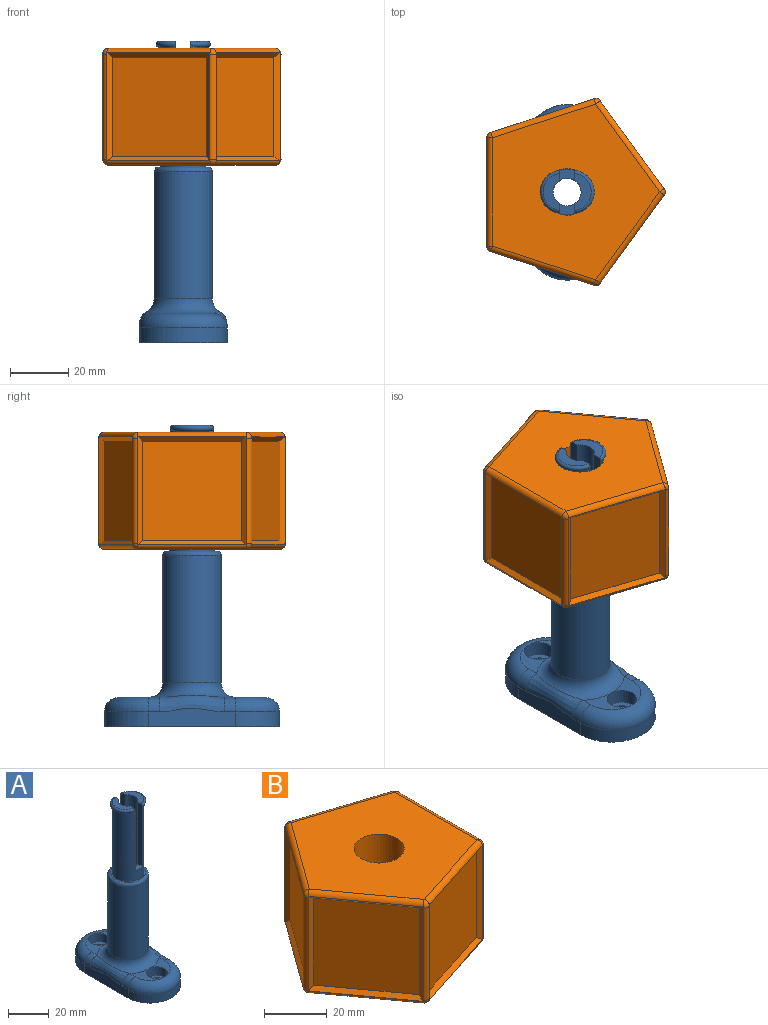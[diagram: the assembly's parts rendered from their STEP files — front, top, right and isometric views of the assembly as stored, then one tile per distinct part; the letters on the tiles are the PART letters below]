
ASSEMBLY  parts=2 mates=1
PART A: 44 faces, bbox 40.2x62.5x103 mm
  f0: cylinder r=4.75mm len=103mm, axis (0,0,-1), area 2685mm2, adj f12,f15,f16,f17,f18,f19,f20,f21
  f1: cylinder r=7.75mm len=42mm, axis (0,0,-1), area 1636.6mm2, adj f14,f15,f16,f17,f18,f19,f20,f22
  f2: plane 13.82x10mm, normal (0,0,1), area 51.3mm2, adj f29,f31,f34,f36
  f3: plane 13.82x10mm, normal (0,0,1), area 51.3mm2, adj f27,f31,f39,f40
  f4: plane 13.82x10mm, normal (0,0,1), area 51.3mm2, adj f29,f31,f33,f34
  f5: cylinder r=3mm len=6mm, axis (0,0,-1), area 94.2mm2, adj f12,f30
  f6: cylinder r=3mm len=6mm, axis (0,0,-1), area 94.2mm2, adj f12,f28
  f7: plane 30x6.34mm, normal (1,0,0), area 164.8mm2, adj f8,f10,f12,f36,f38,f40
  f8: cylinder r=15mm len=30mm, axis (0,0,-1), area 235.6mm2, adj f7,f9,f12,f39
  f9: plane 30x6.34mm, normal (-1,0,0), area 164.8mm2, adj f8,f10,f12,f33,f35,f37
  f10: cylinder r=15mm len=30mm, axis (0,0,-1), area 235.6mm2, adj f7,f9,f12,f34
  f11: plane 13.82x10mm, normal (0,0,1), area 51.3mm2, adj f27,f31,f37,f39
  f12: plane 60x30mm, normal (0,0,-1), area 1479.4mm2, adj f0,f5,f6,f7,f8,f9,f10
  f13: cylinder r=10mm len=43.5mm, axis (0,0,-1), area 2733.2mm2, adj f31,f32
  f14: plane 17x17mm, normal (0,0,1), area 38.3mm2, adj f1,f32
  f15: plane 5x3.71mm, normal (0,0,1), area 15.5mm2, adj f0,f1,f16,f17
  f16: plane 37.04x3.34mm, normal (1,0,0), area 121.8mm2, adj f0,f1,f15,f23,f26
  f17: plane 37.04x3.34mm, normal (-1,0,0), area 121.8mm2, adj f0,f1,f15,f21,f25
  f18: plane 5x3.71mm, normal (0,0,1), area 15.5mm2, adj f0,f1,f19,f20
  f19: plane 37.04x3.34mm, normal (-1,0,0), area 120.9mm2, adj f0,f1,f18,f21,f25,f41
  f20: plane 37.04x3.34mm, normal (1,0,0), area 121.8mm2, adj f0,f1,f18,f23,f26
  f21: plane 12.66x5.75mm, normal (0,0,1), area 43mm2, adj f0,f17,f19,f25
  f22: plane 9.48x2.12mm, normal (0,0,-1), area 3.4mm2, adj f1,f25
  f23: plane 12.66x5.75mm, normal (0,0,1), area 43mm2, adj f0,f16,f20,f26
  f24: plane 9.48x2.12mm, normal (0,0,-1), area 3.4mm2, adj f1,f26
  f25: torus R=6.36mm, axis (0,0,1), area 60.7mm2, adj f1,f17,f19,f21,f22
  f26: torus R=6.36mm, axis (0,0,1), area 60.7mm2, adj f1,f16,f20,f23,f24
  f27: cylinder r=5mm len=10mm, axis (0,0,1), area 157.1mm2, adj f3,f11,f28
  f28: plane 10x10mm, normal (0,0,1), area 50.3mm2, adj f6,f27
  f29: cylinder r=5mm len=10mm, axis (0,0,1), area 157.1mm2, adj f2,f4,f30
  f30: plane 10x10mm, normal (0,0,1), area 50.3mm2, adj f5,f29
  f31: torus R=15mm, axis (0,0,1), area 496.9mm2, adj f2,f3,f4,f11,f13,f35,f38
  f32: torus R=8.5mm, axis (0,0,1), area 140mm2, adj f13,f14
  f33: cylinder r=5mm len=5mm, axis (0,1,0), area 30mm2, adj f4,f9,f34,f35
  f34: torus R=10mm, axis (0,0,1), area 325.3mm2, adj f2,f4,f10,f33,f36
  f35: bspline ~25.73x5.67mm, area 140.1mm2, adj f9,f31,f33,f37
  f36: cylinder r=5mm len=5mm, axis (0,-1,0), area 30mm2, adj f2,f7,f34,f38
  f37: cylinder r=5mm len=5mm, axis (0,1,0), area 30mm2, adj f9,f11,f35,f39
  f38: bspline ~25.73x5.67mm, area 140.1mm2, adj f7,f31,f36,f40
  f39: torus R=10mm, axis (0,0,1), area 325.3mm2, adj f3,f8,f11,f37,f40
  f40: cylinder r=5mm len=5mm, axis (0,-1,0), area 30mm2, adj f3,f7,f38,f39
  f41: cylinder r=1.5mm len=2.07mm, axis (-0.71,-0.71,0), area 0.6mm2, adj f0,f19
  f42: plane 1.68x0.99mm, normal (0.71,0.71,0), area 1.8mm2, adj f43
  f43: bspline ~3x2.13mm, area 6mm2, adj f1,f42
PART B: 65 faces, bbox 61.1x64x40 mm
  f0: cylinder r=8mm len=40mm, axis (0,0,-1), area 2003.5mm2, adj f11,f12,f63
  f1: plane 36x0.04mm, normal (0.31,-0.95,0), area 1.7mm2, adj f21,f42,f43,f53
  f2: plane 36x0.04mm, normal (-0.81,-0.59,0), area 1.7mm2, adj f25,f41,f47,f56
  f3: plane 36x0.05mm, normal (1,0,0), area 1.7mm2, adj f37,f38,f46,f57
  f4: plane 36x0.04mm, normal (-0.81,0.59,0), area 1.7mm2, adj f29,f40,f51,f60
  f5: plane 36x0.04mm, normal (0.31,0.95,0), area 1.7mm2, adj f33,f39,f50,f61
  f6: plane 36x0.04mm, normal (0.31,-0.95,0), area 1.7mm2, adj f18,f41,f43,f53
  f7: plane 36x0.04mm, normal (-0.81,-0.59,0), area 1.7mm2, adj f22,f40,f47,f56
  f8: plane 36x0.04mm, normal (-0.81,0.59,0), area 1.7mm2, adj f26,f39,f51,f60
  f9: plane 36x0.04mm, normal (0.31,0.95,0), area 1.7mm2, adj f30,f38,f50,f61
  f10: plane 36x0.05mm, normal (1,0,0), area 1.7mm2, adj f34,f42,f46,f57
  f11: plane 60.02x57.08mm, normal (0,0,1), area 2166.2mm2, adj f0,f43,f46,f47,f50,f51
  f12: plane 60.02x57.08mm, normal (0,0,-1), area 2166.2mm2, adj f0,f53,f56,f57,f60,f61
  f13: plane 34x34mm, normal (1,0,0), area 1156mm2, adj f34,f35,f36,f37
  f14: plane 34x32.34mm, normal (0.31,0.95,0), area 1156mm2, adj f30,f31,f32,f33
  f15: plane 34x27.51mm, normal (-0.81,0.59,0), area 1156mm2, adj f26,f27,f28,f29
  f16: plane 34x27.51mm, normal (-0.81,-0.59,0), area 1156mm2, adj f22,f23,f24,f25
  f17: plane 34x32.34mm, normal (0.31,-0.95,0), area 1156mm2, adj f18,f19,f20,f21
  f18: plane 36.9x1.89mm, normal (0.89,-0.45,0), area 75.3mm2, adj f6,f17,f19,f20,f43,f53
  f19: plane 35.09x12.33mm, normal (0.22,-0.67,-0.71), area 72.6mm2, adj f17,f18,f21,f43
  f20: plane 35.09x12.33mm, normal (0.22,-0.67,0.71), area 72.6mm2, adj f17,f18,f21,f53
  f21: plane 36.9x1.89mm, normal (-0.45,-0.89,0), area 75.3mm2, adj f1,f17,f19,f20,f43,f53
  f22: plane 36.9x2.1mm, normal (-0.16,-0.99,0), area 75.3mm2, adj f7,f16,f23,f24,f47,f56
  f23: plane 29.85x22.01mm, normal (-0.57,-0.42,-0.71), area 72.6mm2, adj f16,f22,f25,f47
  f24: plane 29.85x22.01mm, normal (-0.57,-0.42,0.71), area 72.6mm2, adj f16,f22,f25,f56
  f25: plane 36.9x2.1mm, normal (-0.99,0.16,0), area 75.3mm2, adj f2,f16,f23,f24,f47,f56
  f26: plane 36.9x2.1mm, normal (-0.99,-0.16,0), area 75.3mm2, adj f8,f15,f27,f28,f51,f60
  f27: plane 29.85x22.01mm, normal (-0.57,0.42,-0.71), area 72.6mm2, adj f15,f26,f29,f51
  f28: plane 29.85x22.01mm, normal (-0.57,0.42,0.71), area 72.6mm2, adj f15,f26,f29,f60
  f29: plane 36.9x2.1mm, normal (-0.16,0.99,0), area 75.3mm2, adj f4,f15,f27,f28,f51,f60
  f30: plane 36.9x1.89mm, normal (-0.45,0.89,0), area 75.3mm2, adj f9,f14,f31,f32,f50,f61
  f31: plane 35.09x12.33mm, normal (0.22,0.67,-0.71), area 72.6mm2, adj f14,f30,f33,f50
  f32: plane 35.09x12.33mm, normal (0.22,0.67,0.71), area 72.6mm2, adj f14,f30,f33,f61
  f33: plane 36.9x1.89mm, normal (0.89,0.45,0), area 75.3mm2, adj f5,f14,f31,f32,f50,f61
  f34: plane 36.9x1.5mm, normal (0.71,0.71,0), area 75.3mm2, adj f10,f13,f35,f36,f46,f57
  f35: plane 36.9x1.45mm, normal (0.71,0,-0.71), area 72.6mm2, adj f13,f34,f37,f46
  f36: plane 36.9x1.45mm, normal (0.71,0,0.71), area 72.6mm2, adj f13,f34,f37,f57
  f37: plane 36.9x1.5mm, normal (0.71,-0.71,0), area 75.3mm2, adj f3,f13,f35,f36,f46,f57
  f38: cylinder r=2mm len=36mm, axis (0,0,-1), area 90.5mm2, adj f3,f9,f48,f59
  f39: cylinder r=2mm len=36mm, axis (0,0,-1), area 90.5mm2, adj f5,f8,f52,f62
  f40: cylinder r=2mm len=36mm, axis (0,0,-1), area 90.5mm2, adj f4,f7,f49,f58
  f41: cylinder r=2mm len=36mm, axis (0,0,-1), area 90.5mm2, adj f2,f6,f45,f54
  f42: cylinder r=2mm len=36mm, axis (0,0,-1), area 90.5mm2, adj f1,f10,f44,f55
  f43: cylinder r=2mm len=35.9mm, axis (-0.95,-0.31,0), area 99.8mm2, adj f1,f6,f11,f18,f19,f21,f44,f45
  f44: sphere r=2mm, area 5mm2, adj f42,f43,f46
  f45: sphere r=2mm, area 5mm2, adj f41,f43,f47
  f46: cylinder r=2mm len=37.09mm, axis (0,-1,0), area 99.8mm2, adj f3,f10,f11,f34,f35,f37,f44,f48
  f47: cylinder r=2mm len=31.19mm, axis (-0.59,0.81,0), area 99.8mm2, adj f2,f7,f11,f22,f23,f25,f45,f49
  f48: sphere r=2mm, area 5mm2, adj f38,f46,f50
  f49: sphere r=2mm, area 5mm2, adj f40,f47,f51
  f50: cylinder r=2mm len=35.9mm, axis (0.95,-0.31,0), area 99.8mm2, adj f5,f9,f11,f30,f31,f33,f48,f52
  f51: cylinder r=2mm len=31.19mm, axis (0.59,0.81,0), area 99.8mm2, adj f4,f8,f11,f26,f27,f29,f49,f52
  f52: sphere r=2mm, area 5mm2, adj f39,f50,f51
  f53: cylinder r=2mm len=35.9mm, axis (0.95,0.31,0), area 99.8mm2, adj f1,f6,f12,f18,f20,f21,f54,f55
  f54: sphere r=2mm, area 5mm2, adj f41,f53,f56
  f55: sphere r=2mm, area 5mm2, adj f42,f53,f57
  f56: cylinder r=2mm len=31.19mm, axis (0.59,-0.81,0), area 99.8mm2, adj f2,f7,f12,f22,f24,f25,f54,f58
  f57: cylinder r=2mm len=37.09mm, axis (0,1,0), area 99.8mm2, adj f3,f10,f12,f34,f36,f37,f55,f59
  f58: sphere r=2mm, area 5mm2, adj f40,f56,f60
  f59: sphere r=2mm, area 5mm2, adj f38,f57,f61
  f60: cylinder r=2mm len=31.19mm, axis (-0.59,-0.81,0), area 99.8mm2, adj f4,f8,f12,f26,f28,f29,f58,f62
  f61: cylinder r=2mm len=35.9mm, axis (-0.95,0.31,0), area 99.8mm2, adj f5,f9,f12,f30,f32,f33,f59,f62
  f62: sphere r=2mm, area 5mm2, adj f39,f60,f61
  f63: cylinder r=1.5mm len=3mm, axis (-1,0,0), area 19.5mm2, adj f0,f64
  f64: plane 3x3mm, normal (-1,0,0), area 7.1mm2, adj f63
PLACE A t=(-43.54,-6.89,-87.62)mm
PLACE B rot(axis=(0,0,1),180deg) t=(-43.54,-6.89,-27)mm
MATE revolute B.f0 <-> A.f1  axis (0,0,-1) through (-43.54,-6.89,13)mm
